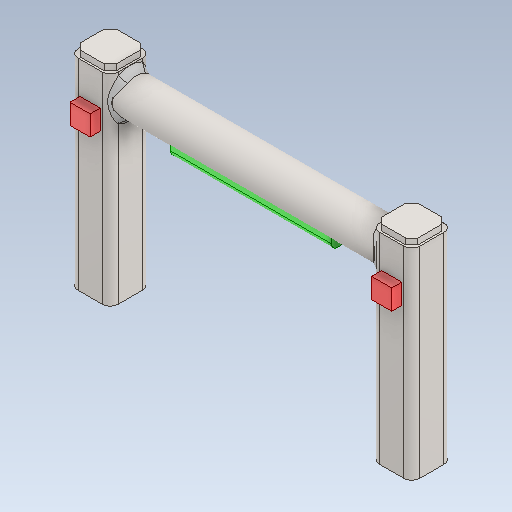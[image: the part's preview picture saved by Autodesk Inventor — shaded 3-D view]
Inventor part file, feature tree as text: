
AUTODESK INVENTOR PART (.ipt)
format: ipt  version: 2021 (Build 250183000, 183)  size: 268,288 bytes
history: mixed  units: mm
features: other x16, fillet x3, surface_op x1, imported_body x1
ambient origin geometry x8: Origin, YZ Plane, XZ Plane, XY Plane, X Axis, Y Axis, Z Axis, Center Point
bodies: Body1 (imported_parasolid), Body2 (imported_parasolid), Body3 (imported_parasolid), Body4 (imported_parasolid), Body5 (imported_parasolid), Body6 (imported_parasolid), Body7 (imported_parasolid), Body8 (imported_parasolid), Body9 (imported_parasolid), Body10 (imported_parasolid)
feature tree (21):
  other  "Sólido1"
  other  "Sólido2"
  other  "Sólido3"
  other  "Sólido4"
  other  "Sólido5"
  other  "Sólido6"
  other  "Sólido7"
  other  "Sólido8"
  other  "Sólido9"
  other  "Sólido10"
  other  "Structural Member4[2]"
  surface_op  "Trim_Extend5"
  fillet  "Fillet Bead4"  [1 undecoded]
  fillet  "Fillet Bead5"  [1 undecoded]
  other  "End cap2[1]"
  other  "End cap2[2]"
  other  "Boss-Extrude1"
  other  "LPattern1"
  fillet  "Fillet1"  [1 undecoded]
  other  "Boss-Extrude4"
  imported_body  NMx_Import_Brep_tag  [imported B-rep: ~23 faces, bbox_mm=None]
note: 3 required parameter values undecoded (feature->parameter linkage not recoverable at this tier; creation-order binding heuristic only, values carry confidence <= 0.55)
